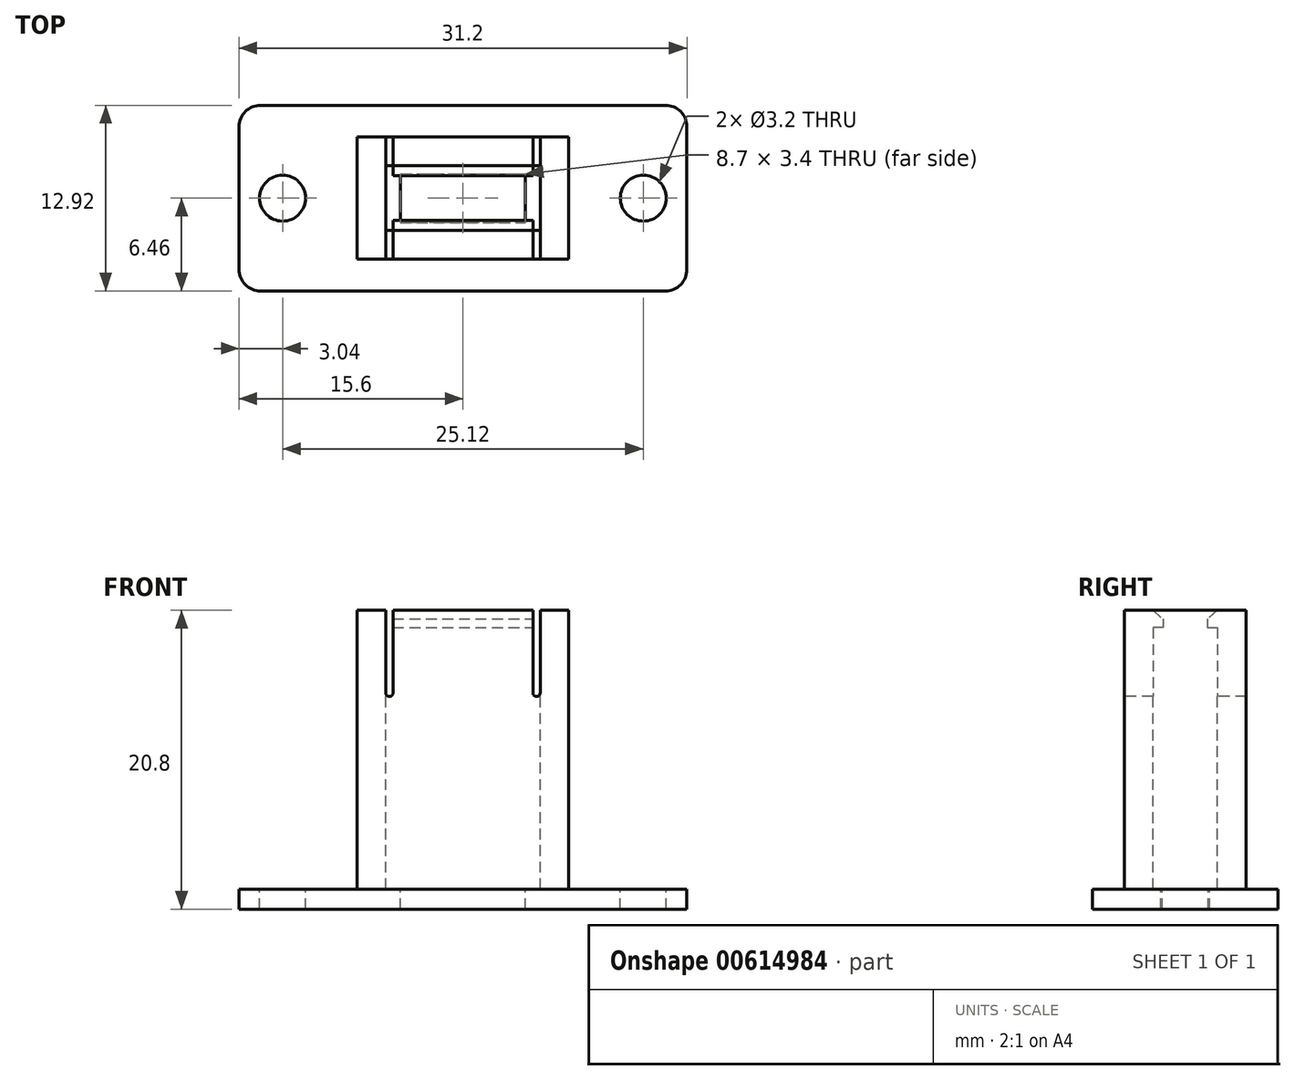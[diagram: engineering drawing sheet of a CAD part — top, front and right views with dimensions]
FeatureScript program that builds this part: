
annotation { "Feature Type Name" : "Feature", "Feature Type Description" : "" }
export const myFeature = defineFeature(function(context is Context, id is Id, definition is map)
    precondition{}
    {
        {
            var Q0;
            Q0=qCreatedBy(makeId("Top.planeOp"),FACE);
            var sketch = newSketch(context, id + "F0", { "sketchPlane" : qUnion([Q0])});
            skLineSegment(sketch, "E0.bottom", {"start": v(-15.6, 6.46) * mm, "end": v(15.6, 6.46) * mm});
            skLineSegment(sketch, "E0.top", {"start": v(-15.6, -6.46) * mm, "end": v(15.6, -6.46) * mm});
            skLineSegment(sketch, "E0.left", {"start": v(-15.6, 6.46) * mm, "end": v(-15.6, -6.46) * mm});
            skLineSegment(sketch, "E0.right", {"start": v(15.6, 6.46) * mm, "end": v(15.6, -6.46) * mm});
            skPoint(sketch, "E1", {"position": v(-15.6, 0) * mm});
            skPoint(sketch, "E2", {"position": v(0, 6.46) * mm});
            skSolve(sketch);
        }
        {
            var Q0;
            Q0=qSketchRegion(id+"F0",true);
            extrude(context, id + "F1", {"entities" : qUnion([Q0]), "depth" : 1.4 * mm, "offsetDistance" : 25 * mm});
        }
        {
            var Q0;
            Q0=makeQuery(id+"F1.opExtrude","CAP_FACE",FACE,{"disambiguationData":[OSD([sQuery(id+"F0.wireOp",EDGE,"E0.bottom"),sQuery(id+"F0.wireOp",EDGE,"E0.top"),sQuery(id+"F0.wireOp",EDGE,"E0.left"),sQuery(id+"F0.wireOp",EDGE,"E0.right")])],"isStart":false});
            var sketch = newSketch(context, id + "F2", { "sketchPlane" : qUnion([Q0])});
            skCircle(sketch, "E3", {"center": v(-12.56, 0) * mm, "radius": 1.6 * mm});
            skCircle(sketch, "E4", {"center": v(12.56, 0) * mm, "radius": 1.6 * mm});
            skSolve(sketch);
        }
        {
            var Q0;
            Q0=qSketchRegion(id+"F2",true);
            extrude(context, id + "F3", {"entities" : qUnion([Q0]), "operationType" : NewBodyOperationType.REMOVE, "endBound" : BoundingType.THROUGH_ALL, "oppositeDirection" : true, "depth" : 25 * mm, "offsetDistance" : 25 * mm});
        }
        {
            var Q0;
            Q0=makeQuery(id+"F1.opExtrude","SWEPT_EDGE",EDGE,{"disambiguationData":[OSD([sQuery(id+"F0.wireOp",EDGE,"E0.top"),sQuery(id+"F0.wireOp",EDGE,"E0.right")])]});
            var Q1;
            Q1=makeQuery(id+"F1.opExtrude","SWEPT_EDGE",EDGE,{"disambiguationData":[OSD([sQuery(id+"F0.wireOp",EDGE,"E0.bottom"),sQuery(id+"F0.wireOp",EDGE,"E0.right")])]});
            var Q2;
            Q2=makeQuery(id+"F1.opExtrude","SWEPT_EDGE",EDGE,{"disambiguationData":[OSD([sQuery(id+"F0.wireOp",EDGE,"E0.top"),sQuery(id+"F0.wireOp",EDGE,"E0.left")])]});
            var Q3;
            Q3=makeQuery(id+"F1.opExtrude","SWEPT_EDGE",EDGE,{"disambiguationData":[OSD([sQuery(id+"F0.wireOp",EDGE,"E0.bottom"),sQuery(id+"F0.wireOp",EDGE,"E0.left")])]});
            fillet(context, id + "F4", {"entities" : qUnion([Q0, Q1, Q2, Q3]), "radius" : 1.5 * mm, "tangentPropagation" : true, "allowEdgeOverflow" : false});
        }
        {
            var Q0;
            Q0=makeQuery(id+"F1.opExtrude","CAP_FACE",FACE,{"disambiguationData":[OSD([sQuery(id+"F0.wireOp",EDGE,"E0.bottom"),sQuery(id+"F0.wireOp",EDGE,"E0.top"),sQuery(id+"F0.wireOp",EDGE,"E0.left"),sQuery(id+"F0.wireOp",EDGE,"E0.right")])],"isStart":false});
            var sketch = newSketch(context, id + "F5", { "sketchPlane" : qUnion([Q0])});
            skLineSegment(sketch, "E5.bottom", {"start": v(-4.35, 1.7) * mm, "end": v(4.35, 1.7) * mm});
            skLineSegment(sketch, "E5.top", {"start": v(-4.35, -1.7) * mm, "end": v(4.35, -1.7) * mm});
            skLineSegment(sketch, "E5.left", {"start": v(-4.35, 1.7) * mm, "end": v(-4.35, -1.7) * mm});
            skLineSegment(sketch, "E5.right", {"start": v(4.35, 1.7) * mm, "end": v(4.35, -1.7) * mm});
            skPoint(sketch, "E6", {"position": v(-4.35, 0) * mm});
            skPoint(sketch, "E7", {"position": v(0, -1.7) * mm});
            skSolve(sketch);
        }
        {
            var Q0;
            Q0=qSketchRegion(id+"F5",true);
            extrude(context, id + "F6", {"entities" : qUnion([Q0]), "operationType" : NewBodyOperationType.REMOVE, "endBound" : BoundingType.THROUGH_ALL, "oppositeDirection" : true, "depth" : 25 * mm, "offsetDistance" : 25 * mm});
        }
        {
            var Q0;
            Q0=makeQuery(id+"F1.opExtrude","CAP_FACE",FACE,{"disambiguationData":[OSD([sQuery(id+"F0.wireOp",EDGE,"E0.bottom"),sQuery(id+"F0.wireOp",EDGE,"E0.top"),sQuery(id+"F0.wireOp",EDGE,"E0.left"),sQuery(id+"F0.wireOp",EDGE,"E0.right")])],"isStart":false});
            var sketch = newSketch(context, id + "F7", { "sketchPlane" : qUnion([Q0])});
            skLineSegment(sketch, "E8.bottom", {"start": v(-7.38, 4.25) * mm, "end": v(7.38, 4.25) * mm});
            skLineSegment(sketch, "E8.top", {"start": v(-7.38, -4.25) * mm, "end": v(7.38, -4.25) * mm});
            skLineSegment(sketch, "E8.left", {"start": v(-7.38, 4.25) * mm, "end": v(-7.38, -4.25) * mm});
            skLineSegment(sketch, "E8.right", {"start": v(7.38, 4.25) * mm, "end": v(7.38, -4.25) * mm});
            skPoint(sketch, "E9", {"position": v(-7.38, 0) * mm});
            skPoint(sketch, "E10", {"position": v(0, -4.25) * mm});
            skSolve(sketch);
        }
        {
            var Q0;
            Q0=qSketchRegion(id+"F7",true);
            extrude(context, id + "F8", {"entities" : qUnion([Q0]), "operationType" : NewBodyOperationType.ADD, "depth" : 19.4 * mm, "offsetDistance" : 25 * mm});
        }
        {
            var Q0;
            Q0=makeQuery(id+"F8.opExtrude","CAP_FACE",FACE,{"disambiguationData":[OSD([sQuery(id+"F7.wireOp",EDGE,"E8.bottom"),sQuery(id+"F7.wireOp",EDGE,"E8.top"),sQuery(id+"F7.wireOp",EDGE,"E8.left"),sQuery(id+"F7.wireOp",EDGE,"E8.right")])],"isStart":false});
            var sketch = newSketch(context, id + "F9", { "sketchPlane" : qUnion([Q0])});
            skLineSegment(sketch, "E11.bottom", {"start": v(-5.38, 2.25) * mm, "end": v(5.38, 2.25) * mm});
            skLineSegment(sketch, "E11.top", {"start": v(-5.38, -2.25) * mm, "end": v(5.38, -2.25) * mm});
            skLineSegment(sketch, "E11.left", {"start": v(-5.38, 2.25) * mm, "end": v(-5.38, -2.25) * mm});
            skLineSegment(sketch, "E11.right", {"start": v(5.38, 2.25) * mm, "end": v(5.38, -2.25) * mm});
            skPoint(sketch, "E12", {"position": v(0, 2.25) * mm});
            skPoint(sketch, "E13", {"position": v(5.38, 0) * mm});
            skSolve(sketch);
        }
        {
            var Q0;
            Q0=qSketchRegion(id+"F9",true);
            var Q1;
            Q1=makeQuery(id+"F1.opExtrude","CAP_FACE",FACE,{"disambiguationData":[OSD([sQuery(id+"F0.wireOp",EDGE,"E0.bottom"),sQuery(id+"F0.wireOp",EDGE,"E0.top"),sQuery(id+"F0.wireOp",EDGE,"E0.left"),sQuery(id+"F0.wireOp",EDGE,"E0.right")])],"isStart":false});
            extrude(context, id + "F10", {"entities" : qUnion([Q0]), "operationType" : NewBodyOperationType.REMOVE, "endBound" : BoundingType.UP_TO_SURFACE, "oppositeDirection" : true, "depth" : 25 * mm, "endBoundEntityFace" : qUnion([Q1]), "offsetDistance" : 25 * mm});
        }
        {
            var Q0;
            Q0=makeQuery(id+"F8.opExtrude","SWEPT_FACE",FACE,{"disambiguationData":[OSD([sQuery(id+"F7.wireOp",EDGE,"E8.top")])]});
            var sketch = newSketch(context, id + "F11", { "sketchPlane" : qUnion([Q0])});
            skLineSegment(sketch, "E14.bottom", {"start": v(-5.38, 20.8) * mm, "end": v(-4.88, 20.8) * mm});
            skLineSegment(sketch, "E14.left", {"start": v(-5.38, 20.8) * mm, "end": v(-5.38, 15.05) * mm});
            skLineSegment(sketch, "E14.right", {"start": v(-4.88, 20.8) * mm, "end": v(-4.88, 15.05) * mm});
            skArc(sketch, "E15", {"start": v(-5.38, 15.05) * mm, "mid": v(-5.12, 14.8) * mm, "end": v(-4.88, 15.05) * mm});
            skLineSegment(sketch, "E16.MirrorCS", {"start": v(5.38, 20.8) * mm, "end": v(4.88, 20.8) * mm});
            skArc(sketch, "E17.MirrorCS", {"start": v(5.38, 15.05) * mm, "mid": v(5.12, 14.8) * mm, "end": v(4.88, 15.05) * mm});
            skLineSegment(sketch, "E18.MirrorCS", {"start": v(5.38, 20.8) * mm, "end": v(5.38, 15.05) * mm});
            skLineSegment(sketch, "E19.MirrorCS", {"start": v(4.88, 20.8) * mm, "end": v(4.88, 15.05) * mm});
            skSolve(sketch);
        }
        {
            var Q0;
            Q0 = qSketchRegion(id + "F11", true);
            extrude(context, id + "F12", {"entities" : qUnion([Q0]), "operationType" : NewBodyOperationType.REMOVE, "endBound" : BoundingType.THROUGH_ALL, "oppositeDirection" : true, "depth" : 25 * mm, "offsetDistance" : 25 * mm});
        }
        {
            var Q0;
            {var subQ0=sQuery(id+"F7.wireOp",EDGE,"E8.top");Q0=makeQuery(id+"F12.boolean.opBoolean","COPY",FACE,{"disambiguationData":[TD([makeQuery(id+"F8.opExtrude","SWEPT_FACE",FACE,{"disambiguationData":[OSD([subQ0])]})])],"derivedFrom":makeQuery(id+"F12.opExtrude","SWEPT_FACE",FACE,{"disambiguationData":[OSD([sQuery(id+"F11.wireOp",EDGE,"E19.MirrorCS")])]})});}
            var sketch = newSketch(context, id + "F13", { "sketchPlane" : qUnion([Q0])});
            skLineSegment(sketch, "E20", {"start": v(-2.25, 20.8) * mm, "end": v(-1.55, 20.2) * mm});
            skLineSegment(sketch, "E21", {"start": v(-1.55, 20.2) * mm, "end": v(-1.55, 19.6) * mm});
            skLineSegment(sketch, "E22", {"start": v(-1.55, 19.6) * mm, "end": v(-2.25, 19.6) * mm});
            skLineSegment(sketch, "E23", {"start": v(-2.25, 19.6) * mm, "end": v(-2.25, 20.8) * mm});
            skLineSegment(sketch, "E24.MirrorCS", {"start": v(2.25, 20.8) * mm, "end": v(1.55, 20.2) * mm});
            skLineSegment(sketch, "E25.MirrorCS", {"start": v(1.55, 20.2) * mm, "end": v(1.55, 19.6) * mm});
            skLineSegment(sketch, "E26.MirrorCS", {"start": v(2.25, 19.6) * mm, "end": v(2.25, 20.8) * mm});
            skLineSegment(sketch, "E27.MirrorCS", {"start": v(1.55, 19.6) * mm, "end": v(2.25, 19.6) * mm});
            skSolve(sketch);
        }
        {
            var Q0;
            Q0 = qSketchRegion(id + "F13", true);
            var Q1;
            {var subQ0=sQuery(id+"F7.wireOp",EDGE,"E8.bottom");Q1=makeQuery(id+"F12.boolean.opBoolean","COPY",FACE,{"disambiguationData":[TD([makeQuery(id+"F8.opExtrude","SWEPT_FACE",FACE,{"disambiguationData":[OSD([subQ0])]})])],"derivedFrom":makeQuery(id+"F12.opExtrude","SWEPT_FACE",FACE,{"disambiguationData":[OSD([sQuery(id+"F11.wireOp",EDGE,"E14.right")])]})});}
            extrude(context, id + "F14", {"entities" : qUnion([Q0]), "operationType" : NewBodyOperationType.ADD, "endBound" : BoundingType.UP_TO_SURFACE, "oppositeDirection" : true, "depth" : 25 * mm, "endBoundEntityFace" : qUnion([Q1]), "offsetDistance" : 25 * mm});
        }
    });
